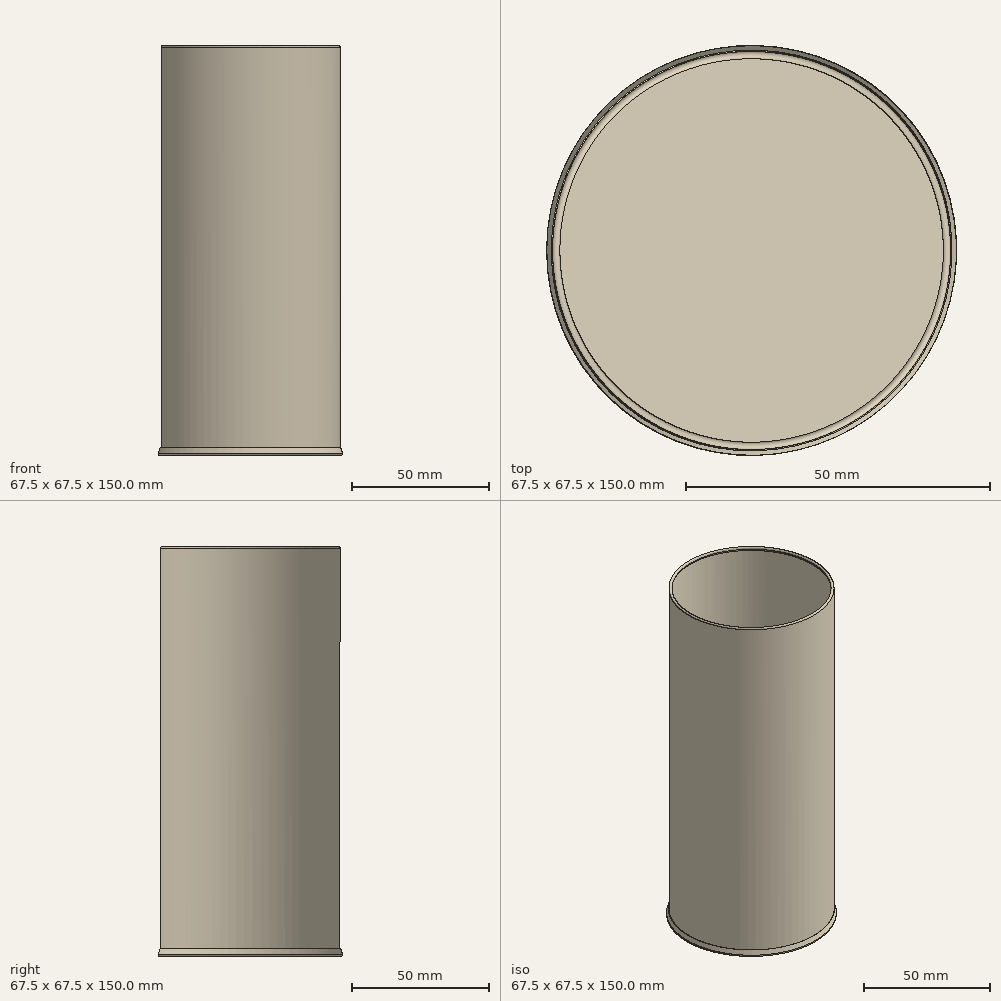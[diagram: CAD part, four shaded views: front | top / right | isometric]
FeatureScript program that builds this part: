
annotation { "Feature Type Name" : "Feature", "Feature Type Description" : "" }
export const myFeature = defineFeature(function(context is Context, id is Id, definition is map)
    precondition{}
    {
        {
            var Q0;
            Q0=qCreatedBy(makeId("Top.planeOp"),FACE);
            var sketch = newSketch(context, id + "F0", { "sketchPlane" : qUnion([Q0])});
            skCircle(sketch, "E0", {"center": v(0, 0) * mm, "radius": 32.75 * mm});
            skSolve(sketch);
        }
        {
            var Q0;
            Q0=makeQuery(id+"F0.imprint","IMPRINT",FACE,{"disambiguationData":[TD([[makeQuery(id+"F0.imprint","IMPRINT",EDGE,{"derivedFrom":sQuery(id+"F0.wireOp",EDGE,"E0")}),1.0]])]});
            extrude(context, id + "F1", {"entities" : qUnion([Q0]), "depth" : (150 - 1.2) * mm, "offsetDistance" : 25.4 * mm});
        }
        {
            var Q0;
            Q0=makeQuery(id+"F1.opExtrude","CAP_FACE",FACE,{"disambiguationData":[OSD([sQuery(id+"F0.wireOp",EDGE,"E0")])],"isStart":false});
            var sketch = newSketch(context, id + "F2", { "sketchPlane" : qUnion([Q0])});
            skCircle(sketch, "E1", {"center": v(0, 0) * mm, "radius": 32.55 * mm});
            skSolve(sketch);
        }
        {
            var Q0;
            Q0 = qSketchRegion(id + "F2", true);
            extrude(context, id + "F3", {"entities" : qUnion([Q0]), "operationType" : NewBodyOperationType.REMOVE, "oppositeDirection" : true, "depth" : 145.2 * mm, "offsetDistance" : 25 * mm});
        }
        {
            var Q0;
            Q0=makeQuery(id+"F1.opExtrude","CAP_FACE",FACE,{"disambiguationData":[OSD([sQuery(id+"F0.wireOp",EDGE,"E0")])],"isStart":true});
            var sketch = newSketch(context, id + "F4", { "sketchPlane" : qUnion([Q0])});
            skCircle(sketch, "E2", {"center": v(0, 0) * mm, "radius": 32 * mm});
            skSolve(sketch);
        }
        {
            var Q0;
            Q0 = qSketchRegion(id + "F4", true);
            extrude(context, id + "F5", {"entities" : qUnion([Q0]), "operationType" : NewBodyOperationType.REMOVE, "oppositeDirection" : true, "depth" : (150 - 146.6) * mm, "offsetDistance" : 25 * mm});
        }
        {
            var Q0;
            Q0=qCreatedBy(makeId("Front.planeOp"),FACE);
            var sketch = newSketch(context, id + "F6", { "sketchPlane" : qUnion([Q0])});
            skArc(sketch, "E3", {"start": v(-33.53, 0.14) * mm, "mid": v(-33.22, -0.4) * mm, "end": v(-32.75, 0) * mm});
            skLineSegment(sketch, "E4", {"start": v(-32.75, 0) * mm, "end": v(-32.55, 0) * mm});
            skLineSegment(sketch, "E5", {"start": v(-33.53, 0.14) * mm, "end": v(-32.8, 2.12) * mm});
            skLineSegment(sketch, "E6", {"start": v(-32.8, 2.12) * mm, "end": v(-32.98, 2.2) * mm});
            skArc(sketch, "E7", {"start": v(-33.71, 0.2) * mm, "mid": v(-33.26, -0.6) * mm, "end": v(-32.55, 0) * mm});
            skLineSegment(sketch, "E8", {"start": v(-33.71, 0.2) * mm, "end": v(-32.98, 2.2) * mm});
            skSolve(sketch);
        }
        {
            var Q0;
            Q0 = qSketchRegion(id + "F6", true);
            var Q1;
            Q1=makeQuery(id+"F1.opExtrude","CAP_EDGE",EDGE,{"disambiguationData":[OSD([sQuery(id+"F0.wireOp",EDGE,"E0")])],"isStart":false});
            revolve(context, id + "F7", {"operationType" : NewBodyOperationType.ADD, "surfaceOperationType" : NewSurfaceOperationType.NEW, "entities" : qUnion([Q0]), "axis" : qUnion([Q1]), "revolveType" : RevolveType.FULL});
        }
        {
            var Q0;
            Q0=qCreatedBy(makeId("Front.planeOp"),FACE);
            var sketch = newSketch(context, id + "F8", { "sketchPlane" : qUnion([Q0])});
            skArc(sketch, "E9", {"start": v(-31.6, 148.58) * mm, "mid": v(-32.04, 149.39) * mm, "end": v(-32.75, 148.8) * mm});
            skArc(sketch, "E10", {"start": v(-31.78, 148.65) * mm, "mid": v(-32.07, 149.2) * mm, "end": v(-32.55, 148.8) * mm});
            skLineSegment(sketch, "E11", {"start": v(-31.78, 148.65) * mm, "end": v(-32.07, 147.9) * mm});
            skLineSegment(sketch, "E12", {"start": v(-32.07, 147.9) * mm, "end": v(-31.89, 147.83) * mm});
            skLineSegment(sketch, "E13", {"start": v(-31.89, 147.83) * mm, "end": v(-31.6, 148.58) * mm});
            skLineSegment(sketch, "E14", {"start": v(-32.75, 148.8) * mm, "end": v(-32.55, 148.8) * mm});
            skSolve(sketch);
        }
        {
            var Q0;
            Q0 = qSketchRegion(id + "F8", true);
            var Q1;
            Q1=makeQuery(id+"F1.opExtrude","CAP_EDGE",EDGE,{"disambiguationData":[OSD([sQuery(id+"F0.wireOp",EDGE,"E0")])],"isStart":false});
            revolve(context, id + "F9", {"operationType" : NewBodyOperationType.ADD, "surfaceOperationType" : NewSurfaceOperationType.NEW, "entities" : qUnion([Q0]), "axis" : qUnion([Q1]), "revolveType" : RevolveType.FULL});
        }
    });
